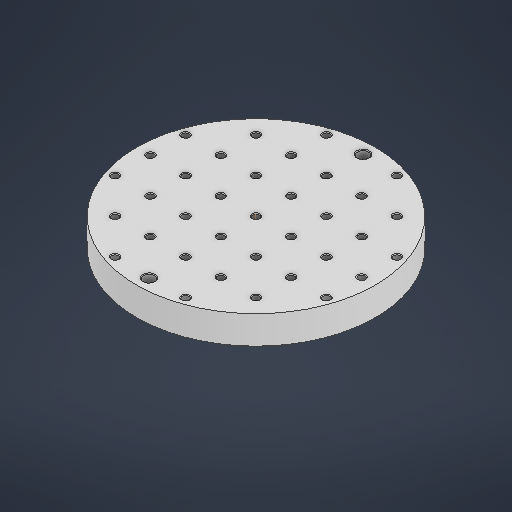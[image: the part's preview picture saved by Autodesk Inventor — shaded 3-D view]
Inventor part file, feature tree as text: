
AUTODESK INVENTOR PART (.ipt)
format: ipt  version: 2025 (Build 290162000, 162)  size: 316,416 bytes
history: native  units: in
note: dims shown in document units (in); Inventor stores cm internally (conversion verified against a paired STEP export)
features: sketch x6, extrude x3, other x1, hole x1, chamfer x1
ambient origin geometry x8: Origin, YZ Plane, XZ Plane, XY Plane, X Axis, Y Axis, Z Axis, Center Point
bodies: Solid1 (feature_tree)
feature tree (12):
  extrude  "Extrusion1"  Depth=0.7874in TaperAngle=0.0deg
  sketch  "Sketch2"  dims[d5=0.315in d6=0.1772in]
  extrude  "Extrusion2"  Depth=0.315in
  extrude  "Extrusion3"  Depth=0.315in
  other  "Work Axis1"
  hole  "Hole1"  [1 undecoded]
  chamfer  "Chamfer2"  Distance=0.4724in
  sketch  "Sketch1"  dims[d0=6.6732in d1=0.7874in d2=0.0in]
  sketch  "Sketch3"  dims[d16=0.2362in]
  sketch  "Sketch Rectangular Pattern1"  dims[d3=5.9843in d4=0.315in]
  sketch  "Sketch Rectangular Pattern2"  dims[d7=0.1772in d8=0.0in d9=0.0in d10=0.4724in d11=0.0in]
  sketch  "Sketch Rectangular Pattern3"  dims[d17=1.1811in d19=0.9843in d20=1.1811in d22=0.9843in d25=0.1936in d26=0.5906in d27=0.2756in d28=0.0787in d29=90.0deg d30=0.5906in d31=0.8108in d32=0.7874in d34=0.9843in d35=1.1811in d37=0.9843in d40=1.1811in d42=0.9843in d43=0.7874in d45=0.9843in d51=0.0197in d52=0.0787in d53=45.0deg]
note: 1 required parameter value undecoded (feature->parameter linkage not recoverable at this tier; creation-order binding heuristic only, values carry confidence <= 0.55)
